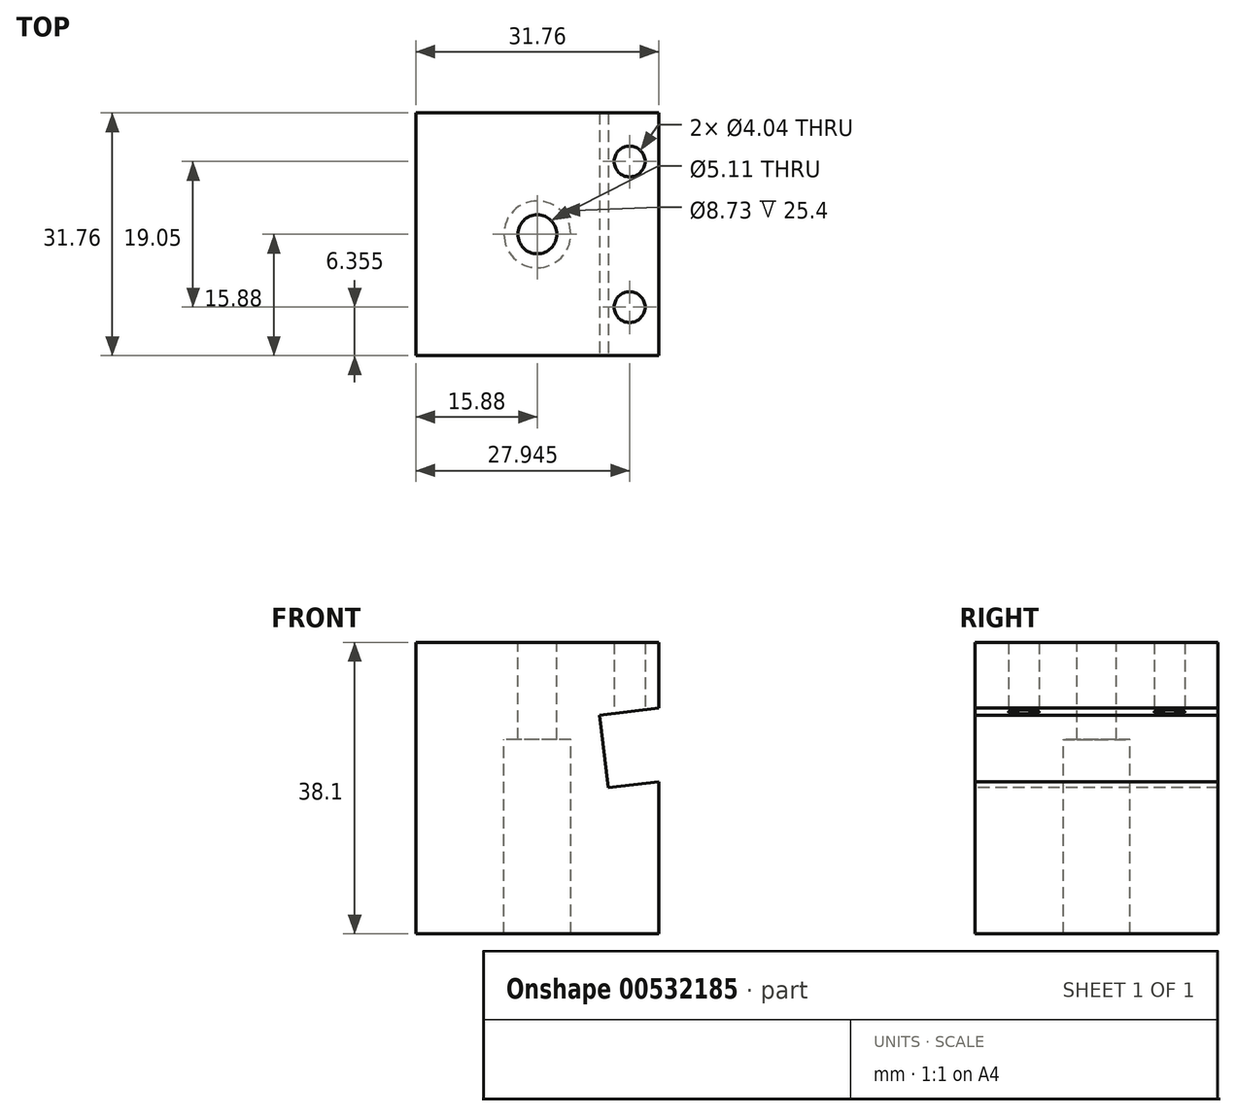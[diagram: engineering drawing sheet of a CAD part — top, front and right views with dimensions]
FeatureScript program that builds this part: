
annotation { "Feature Type Name" : "Feature", "Feature Type Description" : "" }
export const myFeature = defineFeature(function(context is Context, id is Id, definition is map)
    precondition{}
    {
        {
            var Q0;
            Q0=qCreatedBy(makeId("Top.planeOp"),FACE);
            var sketch = newSketch(context, id + "F0", { "sketchPlane" : qUnion([Q0])});
            skLineSegment(sketch, "E0.bottom", {"start": v(15.88, 15.88) * mm, "end": v(-15.88, 15.88) * mm});
            skLineSegment(sketch, "E0.top", {"start": v(15.88, -15.88) * mm, "end": v(-15.88, -15.88) * mm});
            skLineSegment(sketch, "E0.left", {"start": v(15.88, 15.88) * mm, "end": v(15.88, -15.88) * mm});
            skLineSegment(sketch, "E0.right", {"start": v(-15.88, 15.88) * mm, "end": v(-15.88, -15.88) * mm});
            skPoint(sketch, "E0.middle", {"position": v(0, 0) * mm});
            skSolve(sketch);
        }
        {
            var Q0;
            Q0 = qSketchRegion(id + "F0", true);
            extrude(context, id + "F1", {"entities" : qUnion([Q0]), "depth" : 38.1 * mm, "offsetDistance" : 25.4 * mm});
        }
        {
            var Q0;
            Q0=qCreatedBy(makeId("Top.planeOp"),FACE);
            var sketch = newSketch(context, id + "F2", { "sketchPlane" : qUnion([Q0])});
            skPoint(sketch, "E1", {"position": v(0, 0) * mm});
            skSolve(sketch);
        }
        {
            var Q0;
            Q0=sQuery(id+"F2.wireOp",VERTEX,"E1");
            var Q1;
            Q1=makeQuery(id+"F1.opExtrude","SWEPT_BODY",BODY,{"disambiguationData":[OSD([sQuery(id+"F0.wireOp",EDGE,"E0.bottom"),sQuery(id+"F0.wireOp",EDGE,"E0.top"),sQuery(id+"F0.wireOp",EDGE,"E0.left"),sQuery(id+"F0.wireOp",EDGE,"E0.right")])]});
            hole(context, id + "F3", {"style" : HoleStyle.C_BORE, "endStyle" : HoleEndStyle.THROUGH, "oppositeDirection" : true, "standardTappedOrClearance" : lookupTablePath({ "standard" : "ANSI", "size" : "#7 (0.2)", "type" : "Drilled" }), "standardBlindInLast" : lookupTablePath({ "standard" : "ANSI", "size" : "#7", "type" : "Drilled" }), "holeDiameter" : 5.1 * mm, "cBoreDiameter" : 8.73 * mm, "cBoreDepth" : 25.4 * mm, "isTappedThrough" : true, "tappedDepth" : 18.42 * mm, "tapClearance" : 3, "startFromSketch" : true, "locations" : qUnion([Q0]), "scope" : qUnion([Q1])});
        }
        {
            var Q0;
            Q0=makeQuery(id+"F1.opExtrude","SWEPT_FACE",FACE,{"disambiguationData":[OSD([sQuery(id+"F0.wireOp",EDGE,"E0.top")])]});
            var sketch = newSketch(context, id + "F4", { "sketchPlane" : qUnion([Q0])});
            skLineSegment(sketch, "E2", {"start": v(33.32, 31.63) * mm, "end": v(8.11, 28.54) * mm});
            skLineSegment(sketch, "E3", {"start": v(8.11, 28.54) * mm, "end": v(9.27, 19.09) * mm});
            skLineSegment(sketch, "E4", {"start": v(9.27, 19.09) * mm, "end": v(34.48, 22.18) * mm});
            skLineSegment(sketch, "E5", {"start": v(34.48, 22.18) * mm, "end": v(33.32, 31.63) * mm});
            skLineSegment(sketch, "E6", {"start": v(8.7, 23.81) * mm, "end": v(74.38, 23.81) * mm, "construction": true});
            skSolve(sketch);
        }
        {
            var Q0;
            Q0 = qSketchRegion(id + "F4", true);
            extrude(context, id + "F5", {"entities" : qUnion([Q0]), "operationType" : NewBodyOperationType.REMOVE, "endBound" : BoundingType.THROUGH_ALL, "oppositeDirection" : true, "depth" : 25.4 * mm, "offsetDistance" : 25.4 * mm});
        }
        {
            var Q0;
            Q0=makeQuery(id+"F1.opExtrude","CAP_FACE",FACE,{"disambiguationData":[OSD([sQuery(id+"F0.wireOp",EDGE,"E0.bottom"),sQuery(id+"F0.wireOp",EDGE,"E0.top"),sQuery(id+"F0.wireOp",EDGE,"E0.left"),sQuery(id+"F0.wireOp",EDGE,"E0.right")])],"isStart":false});
            var sketch = newSketch(context, id + "F6", { "sketchPlane" : qUnion([Q0])});
            skLineSegment(sketch, "E7", {"start": v(12.07, -9.53) * mm, "end": v(12.07, 9.53) * mm, "construction": true});
            skPoint(sketch, "E8", {"position": v(12.07, 9.53) * mm});
            skPoint(sketch, "E9", {"position": v(12.07, -9.53) * mm});
            skSolve(sketch);
        }
        {
            var Q0;
            Q0=sQuery(id+"F6.wireOp",VERTEX,"E9");
            var Q1;
            Q1=sQuery(id+"F6.wireOp",VERTEX,"E8");
            var Q2;
            Q2=makeQuery(id+"F1.opExtrude","SWEPT_BODY",BODY,{"disambiguationData":[OSD([sQuery(id+"F0.wireOp",EDGE,"E0.bottom"),sQuery(id+"F0.wireOp",EDGE,"E0.top"),sQuery(id+"F0.wireOp",EDGE,"E0.left"),sQuery(id+"F0.wireOp",EDGE,"E0.right")])]});
            hole(context, id + "F7", {"style" : HoleStyle.SIMPLE, "endStyle" : HoleEndStyle.BLIND, "standardTappedOrClearance" : lookupTablePath({ "standard" : "ANSI", "engagement" : "75%", "pitch" : "32 tpi", "size" : "#10", "type" : "Tapped" }), "standardBlindInLast" : lookupTablePath({ "standard" : "ANSI", "engagement" : "75%", "pitch" : "32 tpi", "size" : "#10", "type" : "Tapped" }), "holeDiameter" : 4.04 * mm, "showTappedDepth" : true, "holeDepth" : 9.5 * mm, "isTappedThrough" : true, "tappedDepth" : 7.11 * mm, "tapClearance" : 3, "startFromSketch" : true, "locations" : qUnion([Q0, Q1]), "scope" : qUnion([Q2]), "majorDiameter" : 4.83 * mm});
        }
    });
